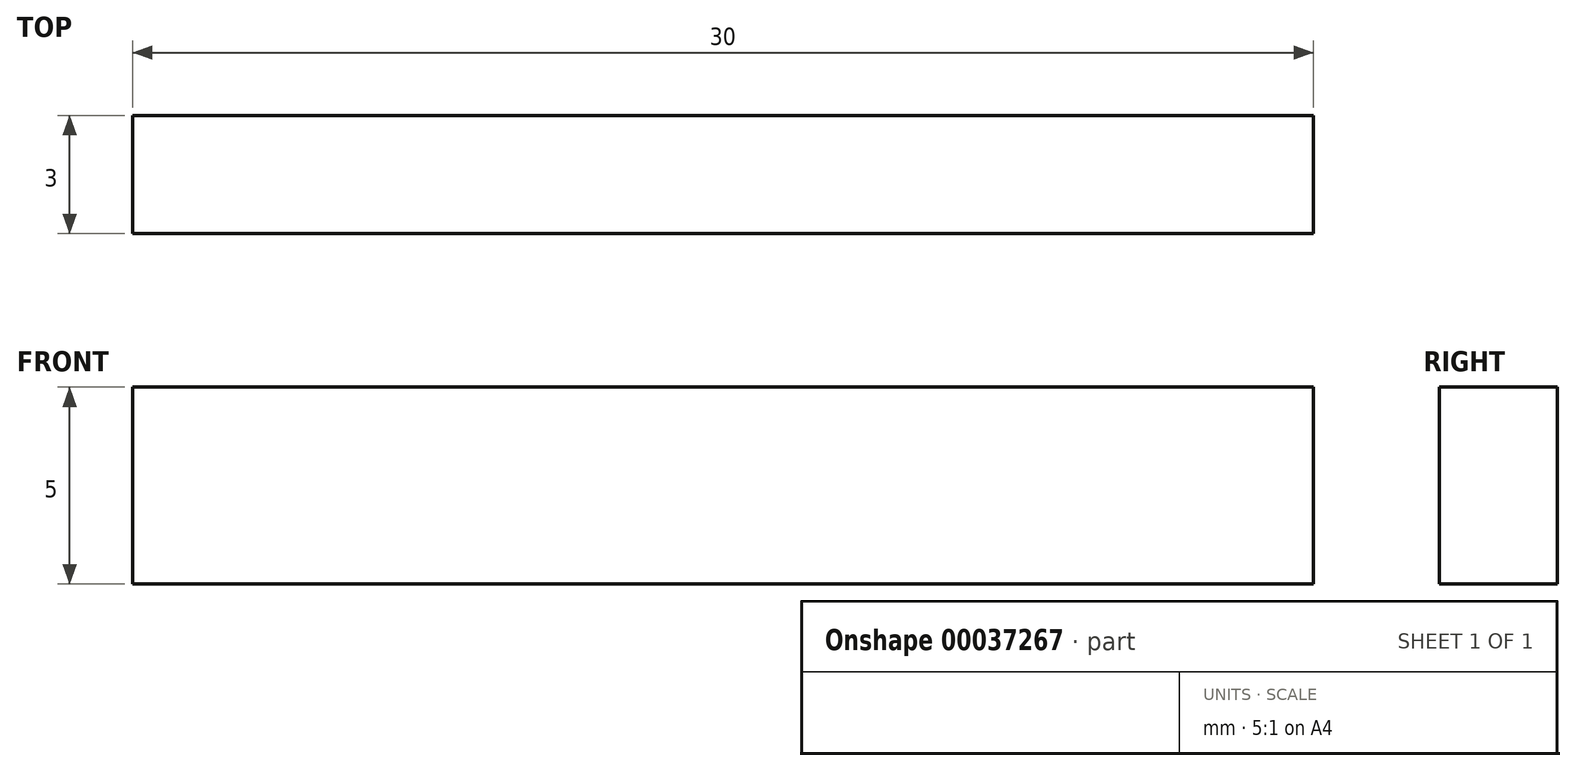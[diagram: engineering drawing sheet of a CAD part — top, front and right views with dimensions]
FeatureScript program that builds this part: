
annotation { "Feature Type Name" : "Feature", "Feature Type Description" : "" }
export const myFeature = defineFeature(function(context is Context, id is Id, definition is map)
    precondition{}
    {
        {
            var Q0;
            Q0=qCreatedBy(makeId("Top.planeOp"),FACE);
            var sketch = newSketch(context, id + "F0", { "sketchPlane" : qUnion([Q0])});
            skLineSegment(sketch, "E0", {"start": v(0, 30) * mm, "end": v(0, -30) * mm, "construction": true});
            skLineSegment(sketch, "E1", {"start": v(-15, 0) * mm, "end": v(15, 0) * mm, "construction": true});
            skLineSegment(sketch, "E2.0", {"start": v(-35.55, -30) * mm, "end": v(28.34, -30) * mm, "construction": true});
            skLineSegment(sketch, "E3.0", {"start": v(-35.55, 30) * mm, "end": v(28.34, 30) * mm, "construction": true});
            skPoint(sketch, "E4.orphan", {"position": v(0, 38.05) * mm});
            skLineSegment(sketch, "E5.0", {"start": v(-15, 30) * mm, "end": v(-15, -30) * mm, "construction": true});
            skLineSegment(sketch, "E6.0", {"start": v(15, 30) * mm, "end": v(15, -30) * mm, "construction": true});
            skPoint(sketch, "E7.orphan", {"position": v(-35.55, 0) * mm});
            skLineSegment(sketch, "E8.0", {"start": v(-15, -1.5) * mm, "end": v(15, -1.5) * mm, "construction": true});
            skLineSegment(sketch, "E9.0", {"start": v(-15, 1.5) * mm, "end": v(15, 1.5) * mm, "construction": true});
            skLineSegment(sketch, "E10", {"start": v(-15, 1.5) * mm, "end": v(-15, -1.5) * mm});
            skLineSegment(sketch, "E11", {"start": v(15, -1.5) * mm, "end": v(15, 1.5) * mm});
            skLineSegment(sketch, "E12", {"start": v(-15, 1.5) * mm, "end": v(15, 1.5) * mm});
            skLineSegment(sketch, "E13", {"start": v(15, -1.5) * mm, "end": v(-15, -1.5) * mm});
            skLineSegment(sketch, "E14", {"start": v(15, 1.5) * mm, "end": v(-15, 30) * mm, "construction": true});
            skLineSegment(sketch, "E15", {"start": v(-15, -1.5) * mm, "end": v(15, -30) * mm, "construction": true});
            skSolve(sketch);
        }
        {
            var Q0;
            Q0=makeQuery(id+"F0.imprint","IMPRINT",FACE,{"disambiguationData":[TD([[makeQuery(id+"F0.imprint","IMPRINT",EDGE,{"derivedFrom":sQuery(id+"F0.wireOp",EDGE,"E10")}),1.0]])]});
            extrude(context, id + "F1", {"entities" : qUnion([Q0]), "depth" : 5 * mm});
        }
    });
